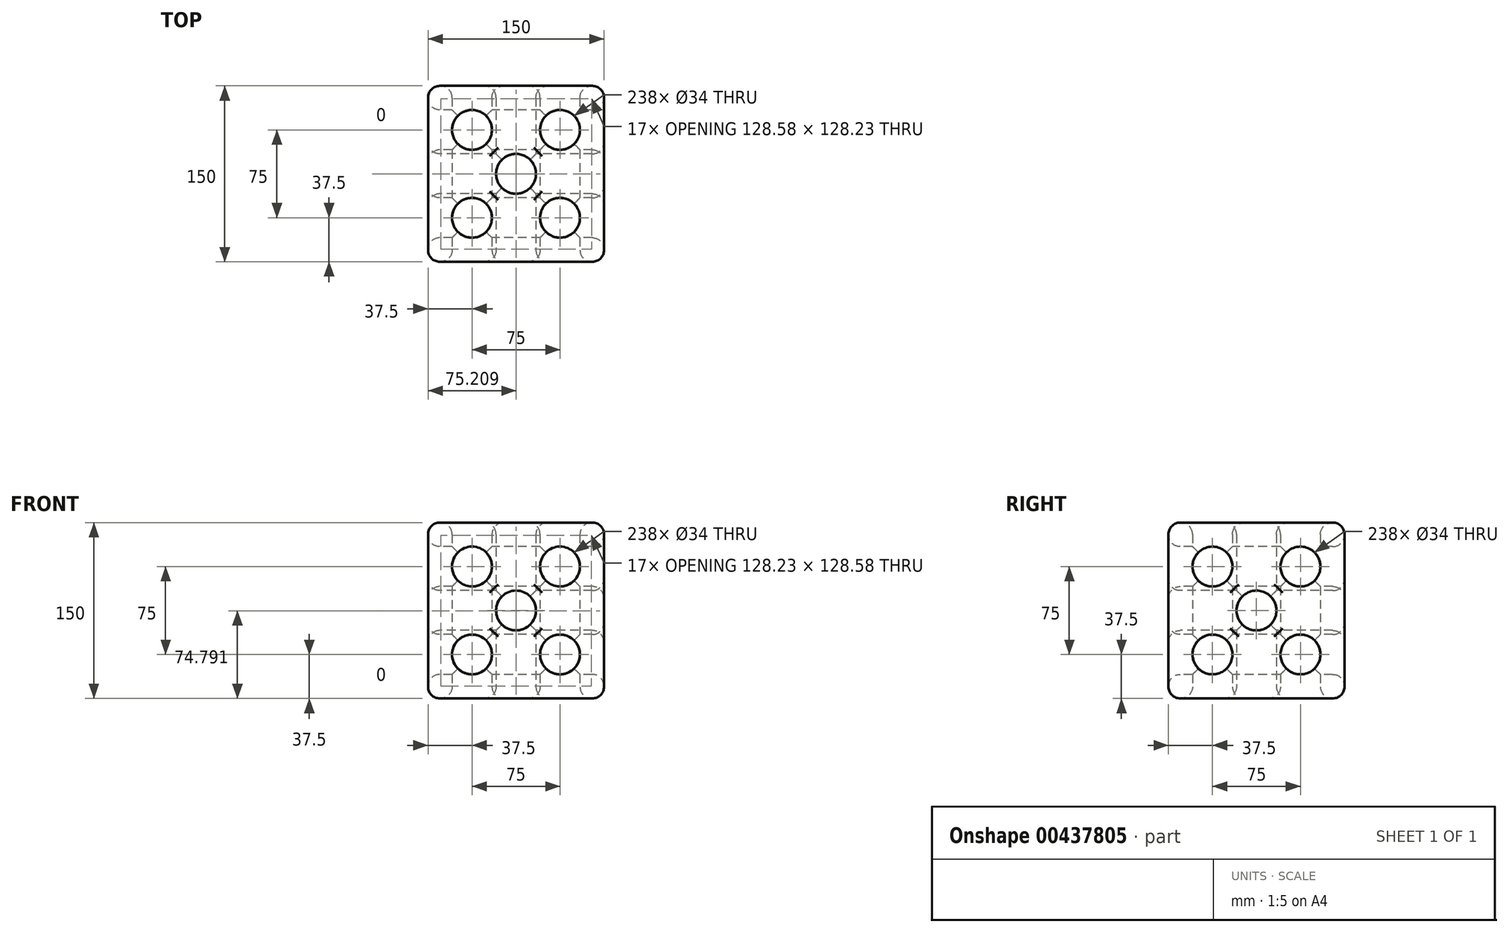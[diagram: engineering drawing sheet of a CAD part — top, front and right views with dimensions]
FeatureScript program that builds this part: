
annotation { "Feature Type Name" : "Feature", "Feature Type Description" : "" }
export const myFeature = defineFeature(function(context is Context, id is Id, definition is map)
    precondition{}
    {
        {
            var Q0;
            Q0=qCreatedBy(makeId("Top.planeOp"),FACE);
            var sketch = newSketch(context, id + "F0", { "sketchPlane" : qUnion([Q0])});
            skLineSegment(sketch, "E0.bottom", {"start": v(75, 75) * mm, "end": v(-75, 75) * mm});
            skLineSegment(sketch, "E0.top", {"start": v(75, -75) * mm, "end": v(-75, -75) * mm});
            skLineSegment(sketch, "E0.left", {"start": v(75, 75) * mm, "end": v(75, -75) * mm});
            skLineSegment(sketch, "E0.right", {"start": v(-75, 75) * mm, "end": v(-75, -75) * mm});
            skPoint(sketch, "E0.middle", {"position": v(0, 0) * mm});
            skCircle(sketch, "E1", {"center": v(0, 0) * mm, "radius": 17 * mm});
            skLineSegment(sketch, "E2", {"start": v(-75, 75) * mm, "end": v(0, 0) * mm, "construction": true});
            skCircle(sketch, "E3", {"center": v(-37.5, 37.5) * mm, "radius": 17 * mm});
            skCircle(sketch, "E4.0.1.0", {"center": v(-37.5, -37.5) * mm, "radius": 17 * mm});
            skCircle(sketch, "E4.1.0.0", {"center": v(37.5, 37.5) * mm, "radius": 17 * mm});
            skCircle(sketch, "E4.1.1.0", {"center": v(37.5, -37.5) * mm, "radius": 17 * mm});
            skLineSegment(sketch, "E4.direction1", {"start": v(-37.5, 37.5) * mm, "end": v(37.5, 37.5) * mm, "construction": true});
            skLineSegment(sketch, "E4.direction2", {"start": v(-37.5, 37.5) * mm, "end": v(-37.5, -37.5) * mm, "construction": true});
            skSolve(sketch);
        }
        {
            var Q0;
            Q0=makeQuery(id+"F0.imprint","IMPRINT",FACE,{"disambiguationData":[TD([[makeQuery(id+"F0.imprint","IMPRINT",EDGE,{"derivedFrom":sQuery(id+"F0.wireOp",EDGE,"E0.bottom")}),1.0]])]});
            extrude(context, id + "F1", {"entities" : qUnion([Q0]), "depth" : 150 * mm});
        }
        {
            var Q0;
            Q0=makeQuery(id+"F1.opExtrude","SWEPT_FACE",FACE,{"disambiguationData":[OSD([sQuery(id+"F0.wireOp",EDGE,"E0.top")])]});
            var sketch = newSketch(context, id + "F2", { "sketchPlane" : qUnion([Q0])});
            skLineSegment(sketch, "E5.bottom", {"start": v(75, 150) * mm, "end": v(-75, 150) * mm});
            skLineSegment(sketch, "E5.top", {"start": v(75, 0) * mm, "end": v(-75, 0) * mm});
            skLineSegment(sketch, "E5.left", {"start": v(75, 150) * mm, "end": v(75, 0) * mm});
            skLineSegment(sketch, "E5.right", {"start": v(-75, 150) * mm, "end": v(-75, 0) * mm});
            skPoint(sketch, "E5.middle", {"position": v(0, 75) * mm});
            skCircle(sketch, "E6", {"center": v(0, 75) * mm, "radius": 17 * mm});
            skLineSegment(sketch, "E7", {"start": v(-75, 150) * mm, "end": v(0, 75) * mm, "construction": true});
            skCircle(sketch, "E8", {"center": v(-37.5, 112.5) * mm, "radius": 17 * mm});
            skCircle(sketch, "E9.0.1.0", {"center": v(-37.5, 37.5) * mm, "radius": 17 * mm});
            skCircle(sketch, "E9.1.0.0", {"center": v(37.5, 112.5) * mm, "radius": 17 * mm});
            skCircle(sketch, "E9.1.1.0", {"center": v(37.5, 37.5) * mm, "radius": 17 * mm});
            skLineSegment(sketch, "E9.direction1", {"start": v(-37.5, 112.5) * mm, "end": v(37.5, 112.5) * mm, "construction": true});
            skLineSegment(sketch, "E9.direction2", {"start": v(-37.5, 112.5) * mm, "end": v(-37.5, 37.5) * mm, "construction": true});
            skSolve(sketch);
        }
        {
            var Q0;
            Q0=makeQuery(id+"F2.imprint","IMPRINT",FACE,{"disambiguationData":[TD([[makeQuery(id+"F2.imprint","IMPRINT",EDGE,{"derivedFrom":sQuery(id+"F2.wireOp",EDGE,"E8")}),1.0]])]});
            var Q1;
            Q1=makeQuery(id+"F2.imprint","IMPRINT",FACE,{"disambiguationData":[TD([[makeQuery(id+"F2.imprint","IMPRINT",EDGE,{"derivedFrom":sQuery(id+"F2.wireOp",EDGE,"E9.0.1.0")}),1.0]])]});
            var Q2;
            Q2=makeQuery(id+"F2.imprint","IMPRINT",FACE,{"disambiguationData":[TD([[makeQuery(id+"F2.imprint","IMPRINT",EDGE,{"derivedFrom":sQuery(id+"F2.wireOp",EDGE,"E6")}),1.0]])]});
            var Q3;
            Q3=makeQuery(id+"F2.imprint","IMPRINT",FACE,{"disambiguationData":[TD([[makeQuery(id+"F2.imprint","IMPRINT",EDGE,{"derivedFrom":sQuery(id+"F2.wireOp",EDGE,"E9.1.1.0")}),1.0]])]});
            var Q4;
            Q4=makeQuery(id+"F2.imprint","IMPRINT",FACE,{"disambiguationData":[TD([[makeQuery(id+"F2.imprint","IMPRINT",EDGE,{"derivedFrom":sQuery(id+"F2.wireOp",EDGE,"E9.1.0.0")}),1.0]])]});
            extrude(context, id + "F3", {"entities" : qUnion([Q0, Q1, Q2, Q3, Q4]), "operationType" : NewBodyOperationType.REMOVE, "oppositeDirection" : true, "depth" : 150 * mm});
        }
        {
            var Q0;
            Q0=makeQuery(id+"F1.opExtrude","SWEPT_FACE",FACE,{"disambiguationData":[OSD([sQuery(id+"F0.wireOp",EDGE,"E0.right")])]});
            var sketch = newSketch(context, id + "F4", { "sketchPlane" : qUnion([Q0])});
            skLineSegment(sketch, "E10.bottom", {"start": v(75, 150) * mm, "end": v(-75, 150) * mm});
            skLineSegment(sketch, "E10.top", {"start": v(75, 0) * mm, "end": v(-75, 0) * mm});
            skLineSegment(sketch, "E10.left", {"start": v(75, 150) * mm, "end": v(75, 0) * mm});
            skLineSegment(sketch, "E10.right", {"start": v(-75, 150) * mm, "end": v(-75, 0) * mm});
            skPoint(sketch, "E10.middle", {"position": v(0, 75) * mm});
            skCircle(sketch, "E11", {"center": v(0, 75) * mm, "radius": 17 * mm});
            skLineSegment(sketch, "E12", {"start": v(-75, 150) * mm, "end": v(0, 75) * mm, "construction": true});
            skCircle(sketch, "E13", {"center": v(-37.5, 112.5) * mm, "radius": 17 * mm});
            skCircle(sketch, "E14.0.1.0", {"center": v(-37.5, 37.5) * mm, "radius": 17 * mm});
            skCircle(sketch, "E14.1.0.0", {"center": v(37.5, 112.5) * mm, "radius": 17 * mm});
            skCircle(sketch, "E14.1.1.0", {"center": v(37.5, 37.5) * mm, "radius": 17 * mm});
            skLineSegment(sketch, "E14.direction1", {"start": v(-37.5, 112.5) * mm, "end": v(37.5, 112.5) * mm, "construction": true});
            skLineSegment(sketch, "E14.direction2", {"start": v(-37.5, 112.5) * mm, "end": v(-37.5, 37.5) * mm, "construction": true});
            skSolve(sketch);
        }
        {
            var Q0;
            Q0=makeQuery(id+"F4.imprint","IMPRINT",FACE,{"disambiguationData":[TD([[makeQuery(id+"F4.imprint","IMPRINT",EDGE,{"derivedFrom":sQuery(id+"F4.wireOp",EDGE,"E14.0.1.0")}),1.0]])]});
            var Q1;
            Q1=makeQuery(id+"F4.imprint","IMPRINT",FACE,{"disambiguationData":[TD([[makeQuery(id+"F4.imprint","IMPRINT",EDGE,{"derivedFrom":sQuery(id+"F4.wireOp",EDGE,"E11")}),1.0]])]});
            var Q2;
            Q2=makeQuery(id+"F4.imprint","IMPRINT",FACE,{"disambiguationData":[TD([[makeQuery(id+"F4.imprint","IMPRINT",EDGE,{"derivedFrom":sQuery(id+"F4.wireOp",EDGE,"E13")}),1.0]])]});
            var Q3;
            Q3=makeQuery(id+"F4.imprint","IMPRINT",FACE,{"disambiguationData":[TD([[makeQuery(id+"F4.imprint","IMPRINT",EDGE,{"derivedFrom":sQuery(id+"F4.wireOp",EDGE,"E14.1.0.0")}),1.0]])]});
            var Q4;
            Q4=makeQuery(id+"F4.imprint","IMPRINT",FACE,{"disambiguationData":[TD([[makeQuery(id+"F4.imprint","IMPRINT",EDGE,{"derivedFrom":sQuery(id+"F4.wireOp",EDGE,"E14.1.1.0")}),1.0]])]});
            extrude(context, id + "F5", {"entities" : qUnion([Q0, Q1, Q2, Q3, Q4]), "operationType" : NewBodyOperationType.REMOVE, "oppositeDirection" : true, "depth" : 150 * mm});
        }
        {
            var Q0;
            Q0=makeQuery(id+"F1.opExtrude","SWEPT_FACE",FACE,{"disambiguationData":[OSD([sQuery(id+"F0.wireOp",EDGE,"E0.left")])]});
            var Q1;
            Q1=makeQuery(id+"F1.opExtrude","CAP_FACE",FACE,{"disambiguationData":[OSD([sQuery(id+"F0.wireOp",EDGE,"E0.bottom"),sQuery(id+"F0.wireOp",EDGE,"E0.top"),sQuery(id+"F0.wireOp",EDGE,"E0.left"),sQuery(id+"F0.wireOp",EDGE,"E0.right"),sQuery(id+"F0.wireOp",EDGE,"E1"),sQuery(id+"F0.wireOp",EDGE,"E3"),sQuery(id+"F0.wireOp",EDGE,"E4.0.1.0"),sQuery(id+"F0.wireOp",EDGE,"E4.1.0.0"),sQuery(id+"F0.wireOp",EDGE,"E4.1.1.0")])],"isStart":false});
            var Q2;
            Q2=makeQuery(id+"F1.opExtrude","SWEPT_FACE",FACE,{"disambiguationData":[OSD([sQuery(id+"F0.wireOp",EDGE,"E0.top")])]});
            var Q3;
            Q3=makeQuery(id+"F1.opExtrude","CAP_FACE",FACE,{"disambiguationData":[OSD([sQuery(id+"F0.wireOp",EDGE,"E0.bottom"),sQuery(id+"F0.wireOp",EDGE,"E0.top"),sQuery(id+"F0.wireOp",EDGE,"E0.left"),sQuery(id+"F0.wireOp",EDGE,"E0.right"),sQuery(id+"F0.wireOp",EDGE,"E1"),sQuery(id+"F0.wireOp",EDGE,"E3"),sQuery(id+"F0.wireOp",EDGE,"E4.0.1.0"),sQuery(id+"F0.wireOp",EDGE,"E4.1.0.0"),sQuery(id+"F0.wireOp",EDGE,"E4.1.1.0")])],"isStart":true});
            var Q4;
            Q4=makeQuery(id+"F1.opExtrude","SWEPT_FACE",FACE,{"disambiguationData":[OSD([sQuery(id+"F0.wireOp",EDGE,"E0.bottom")])]});
            var Q5;
            Q5=makeQuery(id+"F1.opExtrude","SWEPT_FACE",FACE,{"disambiguationData":[OSD([sQuery(id+"F0.wireOp",EDGE,"E0.right")])]});
            fillet(context, id + "F6", {"entities" : qUnion([Q0, Q1, Q2, Q3, Q4, Q5]), "radius" : 10 * mm, "tangentPropagation" : true, "allowEdgeOverflow" : false});
        }
    });
